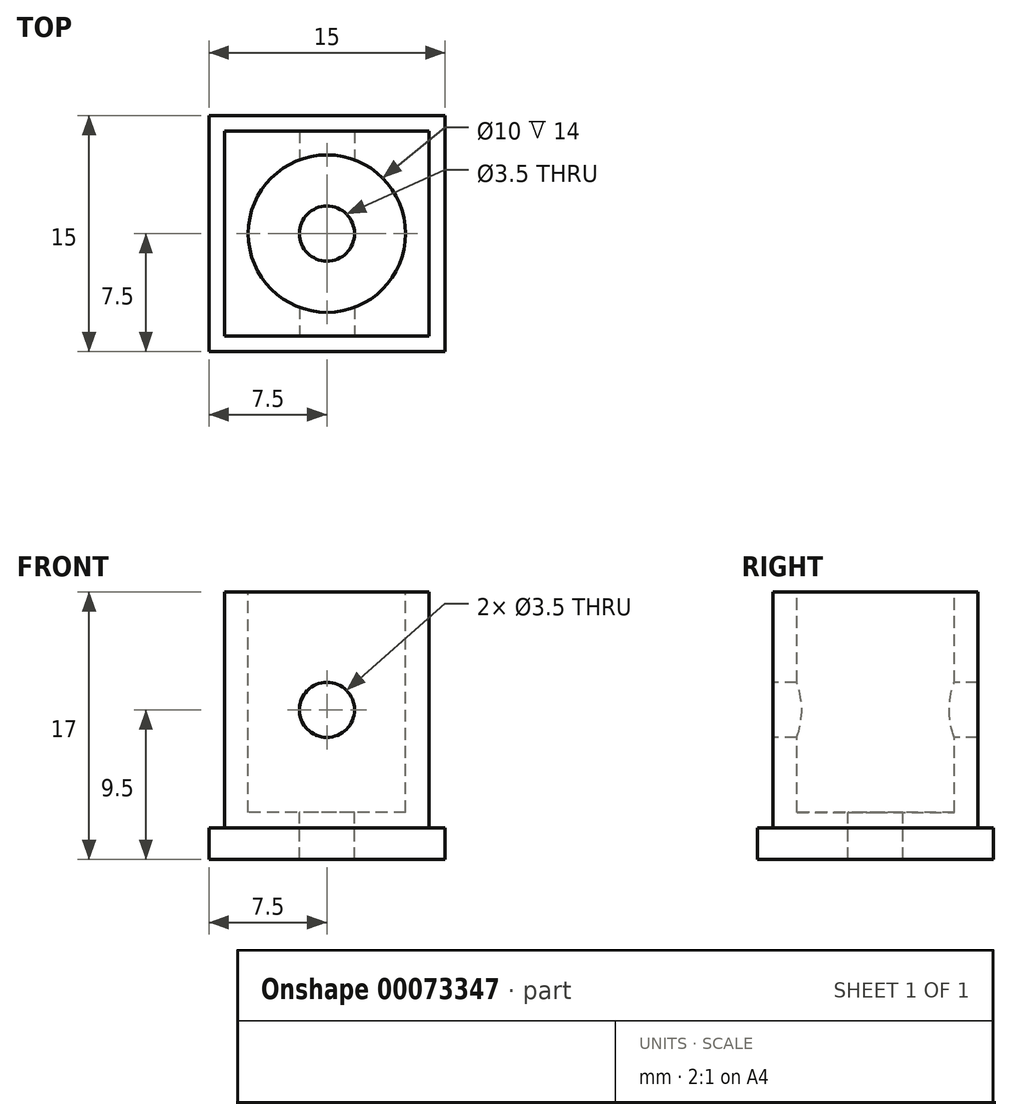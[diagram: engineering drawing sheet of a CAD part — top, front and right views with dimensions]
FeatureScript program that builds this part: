
annotation { "Feature Type Name" : "Feature", "Feature Type Description" : "" }
export const myFeature = defineFeature(function(context is Context, id is Id, definition is map)
    precondition{}
    {
        {
            var Q0;
            Q0=qCreatedBy(makeId("Top.planeOp"),FACE);
            var sketch = newSketch(context, id + "F0", { "sketchPlane" : qUnion([Q0])});
            skLineSegment(sketch, "E0.bottom", {"start": v(-7.5, 7.5) * mm, "end": v(7.5, 7.5) * mm});
            skLineSegment(sketch, "E0.top", {"start": v(-7.5, -7.5) * mm, "end": v(7.5, -7.5) * mm});
            skLineSegment(sketch, "E0.left", {"start": v(-7.5, 7.5) * mm, "end": v(-7.5, -7.5) * mm});
            skLineSegment(sketch, "E0.right", {"start": v(7.5, 7.5) * mm, "end": v(7.5, -7.5) * mm});
            skLineSegment(sketch, "E1", {"start": v(-7.5, 7.5) * mm, "end": v(7.5, -7.5) * mm});
            skPoint(sketch, "E2", {"position": v(0, 0) * mm});
            skSolve(sketch);
        }
        {
            var Q0;
            Q0=makeQuery(id+"F0.imprint","IMPRINT",FACE,{"disambiguationData":[TD([[makeQuery(id+"F0.imprint","IMPRINT",EDGE,{"derivedFrom":sQuery(id+"F0.wireOp",EDGE,"E0.top")}),1.0]])]});
            var Q1;
            Q1=makeQuery(id+"F0.imprint","IMPRINT",FACE,{"disambiguationData":[TD([[makeQuery(id+"F0.imprint","IMPRINT",EDGE,{"derivedFrom":sQuery(id+"F0.wireOp",EDGE,"E0.bottom")}),-1.0]])]});
            extrude(context, id + "F1", {"entities" : qUnion([Q0, Q1]), "depth" : 2 * mm});
        }
        {
            var Q0;
            Q0=makeQuery(id+"F1.opExtrude","CAP_FACE",FACE,{"disambiguationData":[OSD([sQuery(id+"F0.wireOp",EDGE,"E0.bottom"),sQuery(id+"F0.wireOp",EDGE,"E0.top"),sQuery(id+"F0.wireOp",EDGE,"E0.left"),sQuery(id+"F0.wireOp",EDGE,"E0.right")])],"isStart":false});
            var sketch = newSketch(context, id + "F2", { "sketchPlane" : qUnion([Q0])});
            skLineSegment(sketch, "E3.bottom", {"start": v(-6.5, 6.5) * mm, "end": v(6.5, 6.5) * mm});
            skLineSegment(sketch, "E3.top", {"start": v(-6.5, -6.5) * mm, "end": v(6.5, -6.5) * mm});
            skLineSegment(sketch, "E3.left", {"start": v(-6.5, 6.5) * mm, "end": v(-6.5, -6.5) * mm});
            skLineSegment(sketch, "E3.right", {"start": v(6.5, 6.5) * mm, "end": v(6.5, -6.5) * mm});
            skLineSegment(sketch, "E4", {"start": v(-6.5, 6.5) * mm, "end": v(6.5, -6.5) * mm});
            skPoint(sketch, "E5", {"position": v(0, 0) * mm});
            skSolve(sketch);
        }
        {
            var Q0;
            Q0=makeQuery(id+"F2.imprint","IMPRINT",FACE,{"disambiguationData":[TD([[makeQuery(id+"F2.imprint","IMPRINT",EDGE,{"derivedFrom":sQuery(id+"F2.wireOp",EDGE,"E3.top")}),1.0]])]});
            var Q1;
            Q1=makeQuery(id+"F2.imprint","IMPRINT",FACE,{"disambiguationData":[TD([[makeQuery(id+"F2.imprint","IMPRINT",EDGE,{"derivedFrom":sQuery(id+"F2.wireOp",EDGE,"E3.bottom")}),-1.0]])]});
            extrude(context, id + "F3", {"entities" : qUnion([Q0, Q1]), "operationType" : NewBodyOperationType.ADD, "depth" : 15 * mm});
        }
        {
            var Q0;
            Q0=makeQuery(id+"F3.opExtrude","CAP_FACE",FACE,{"disambiguationData":[OSD([sQuery(id+"F2.wireOp",EDGE,"E3.bottom"),sQuery(id+"F2.wireOp",EDGE,"E3.top"),sQuery(id+"F2.wireOp",EDGE,"E3.left"),sQuery(id+"F2.wireOp",EDGE,"E3.right")])],"isStart":false});
            var sketch = newSketch(context, id + "F4", { "sketchPlane" : qUnion([Q0])});
            skPoint(sketch, "E6", {"position": v(0, 0) * mm});
            skSolve(sketch);
        }
        {
            var Q0;
            Q0=sQuery(id+"F4.wireOp",VERTEX,"E6");
            var Q1;
            Q1=makeQuery(id+"F1.opExtrude","SWEPT_BODY",BODY,{"disambiguationData":[OSD([sQuery(id+"F0.wireOp",EDGE,"E0.bottom"),sQuery(id+"F0.wireOp",EDGE,"E0.top"),sQuery(id+"F0.wireOp",EDGE,"E0.left"),sQuery(id+"F0.wireOp",EDGE,"E0.right")])]});
            hole(context, id + "F5", {"style" : HoleStyle.C_BORE, "holeDiameter" : 3.5 * mm, "cBoreDiameter" : 10 * mm, "cBoreDepth" : 14 * mm, "endStyle" : HoleEndStyle.THROUGH, "locations" : qUnion([Q0]), "scope" : qUnion([Q1])});
        }
        {
            var Q0;
            Q0=makeQuery(id+"F3.opExtrude","SWEPT_FACE",FACE,{"disambiguationData":[OSD([sQuery(id+"F2.wireOp",EDGE,"E3.top")])]});
            var sketch = newSketch(context, id + "F6", { "sketchPlane" : qUnion([Q0])});
            skLineSegment(sketch, "E7", {"start": v(-6.5, 17) * mm, "end": v(6.5, 2) * mm});
            skPoint(sketch, "E8", {"position": v(0, 9.5) * mm});
            skSolve(sketch);
        }
        {
            var Q0;
            Q0=sQuery(id+"F6.wireOp",VERTEX,"E8");
            var Q1;
            Q1=makeQuery(id+"F1.opExtrude","SWEPT_BODY",BODY,{"disambiguationData":[OSD([sQuery(id+"F0.wireOp",EDGE,"E0.bottom"),sQuery(id+"F0.wireOp",EDGE,"E0.top"),sQuery(id+"F0.wireOp",EDGE,"E0.left"),sQuery(id+"F0.wireOp",EDGE,"E0.right")])]});
            hole(context, id + "F7", {"style" : HoleStyle.SIMPLE, "holeDiameter" : 3.5 * mm, "endStyle" : HoleEndStyle.THROUGH, "locations" : qUnion([Q0]), "scope" : qUnion([Q1])});
        }
    });
